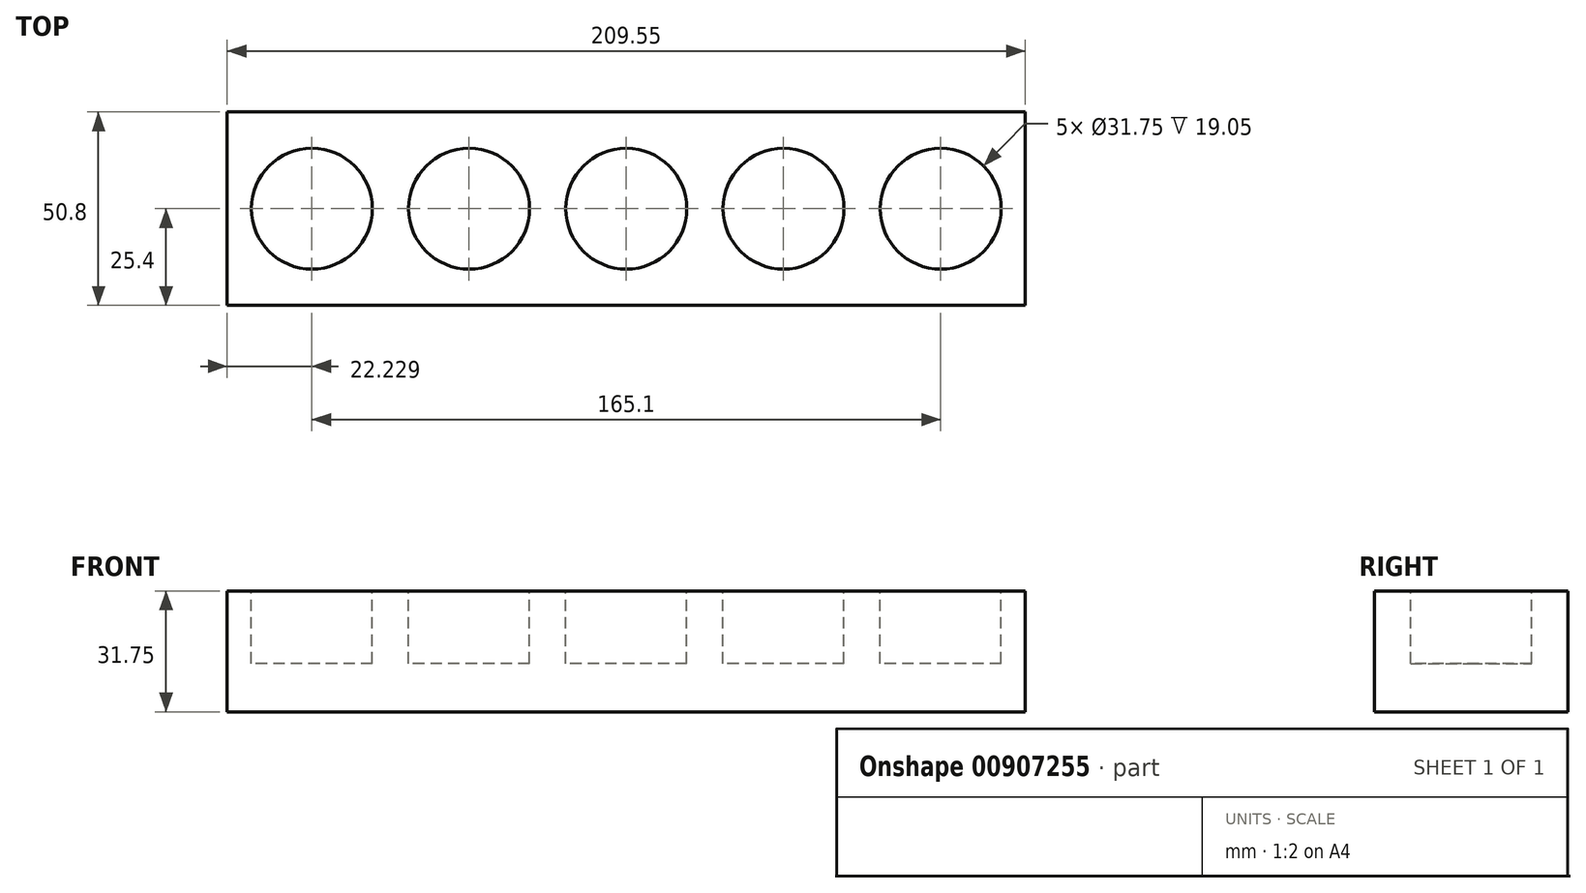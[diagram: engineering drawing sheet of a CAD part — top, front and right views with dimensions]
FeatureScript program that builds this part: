
annotation { "Feature Type Name" : "Feature", "Feature Type Description" : "" }
export const myFeature = defineFeature(function(context is Context, id is Id, definition is map)
    precondition{}
    {
        {
            var Q0;
            Q0=qCreatedBy(makeId("Front.planeOp"),FACE);
            var sketch = newSketch(context, id + "F0", { "sketchPlane" : qUnion([Q0])});
            skLineSegment(sketch, "E0.bottom", {"start": v(-76.09, 0) * mm, "end": v(133.46, 0) * mm});
            skLineSegment(sketch, "E0.top", {"start": v(-76.09, 31.75) * mm, "end": v(133.46, 31.75) * mm});
            skLineSegment(sketch, "E0.left", {"start": v(-76.09, 0) * mm, "end": v(-76.09, 31.75) * mm});
            skLineSegment(sketch, "E0.right", {"start": v(133.46, 0) * mm, "end": v(133.46, 31.75) * mm});
            skSolve(sketch);
        }
        {
            var Q0;
            Q0=makeQuery(id+"F0.imprint","IMPRINT",FACE,{"disambiguationData":[TD([[makeQuery(id+"F0.imprint","IMPRINT",EDGE,{"derivedFrom":sQuery(id+"F0.wireOp",EDGE,"E0.bottom")}),1.0]])]});
            extrude(context, id + "F1", {"entities" : qUnion([Q0]), "depth" : 50.8 * mm, "offsetDistance" : 25.4 * mm});
        }
        {
            var Q0;
            Q0=makeQuery(id+"F1.opExtrude","SWEPT_FACE",FACE,{"disambiguationData":[OSD([sQuery(id+"F0.wireOp",EDGE,"E0.top")])]});
            var sketch = newSketch(context, id + "F2", { "sketchPlane" : qUnion([Q0])});
            skCircle(sketch, "E1", {"center": v(-53.86, -25.4) * mm, "radius": 15.88 * mm});
            skCircle(sketch, "E2", {"center": v(-12.59, -25.4) * mm, "radius": 15.88 * mm});
            skCircle(sketch, "E3", {"center": v(28.69, -25.4) * mm, "radius": 15.88 * mm});
            skCircle(sketch, "E4", {"center": v(69.96, -25.4) * mm, "radius": 15.88 * mm});
            skCircle(sketch, "E5", {"center": v(111.24, -25.4) * mm, "radius": 15.88 * mm});
            skSolve(sketch);
        }
        {
            var Q0;
            Q0=makeQuery(id+"F2.imprint","IMPRINT",FACE,{"disambiguationData":[TD([[makeQuery(id+"F2.imprint","IMPRINT",EDGE,{"derivedFrom":sQuery(id+"F2.wireOp",EDGE,"E1")}),1.0]])]});
            var Q1;
            Q1=makeQuery(id+"F2.imprint","IMPRINT",FACE,{"disambiguationData":[TD([[makeQuery(id+"F2.imprint","IMPRINT",EDGE,{"derivedFrom":sQuery(id+"F2.wireOp",EDGE,"E2")}),1.0]])]});
            var Q2;
            Q2=makeQuery(id+"F2.imprint","IMPRINT",FACE,{"disambiguationData":[TD([[makeQuery(id+"F2.imprint","IMPRINT",EDGE,{"derivedFrom":sQuery(id+"F2.wireOp",EDGE,"E3")}),1.0]])]});
            var Q3;
            Q3=makeQuery(id+"F2.imprint","IMPRINT",FACE,{"disambiguationData":[TD([[makeQuery(id+"F2.imprint","IMPRINT",EDGE,{"derivedFrom":sQuery(id+"F2.wireOp",EDGE,"E4")}),1.0]])]});
            var Q4;
            Q4=makeQuery(id+"F2.imprint","IMPRINT",FACE,{"disambiguationData":[TD([[makeQuery(id+"F2.imprint","IMPRINT",EDGE,{"derivedFrom":sQuery(id+"F2.wireOp",EDGE,"E5")}),1.0]])]});
            extrude(context, id + "F3", {"entities" : qUnion([Q0, Q1, Q2, Q3, Q4]), "operationType" : NewBodyOperationType.REMOVE, "oppositeDirection" : true, "depth" : 19.05 * mm, "offsetDistance" : 25.4 * mm});
        }
    });
